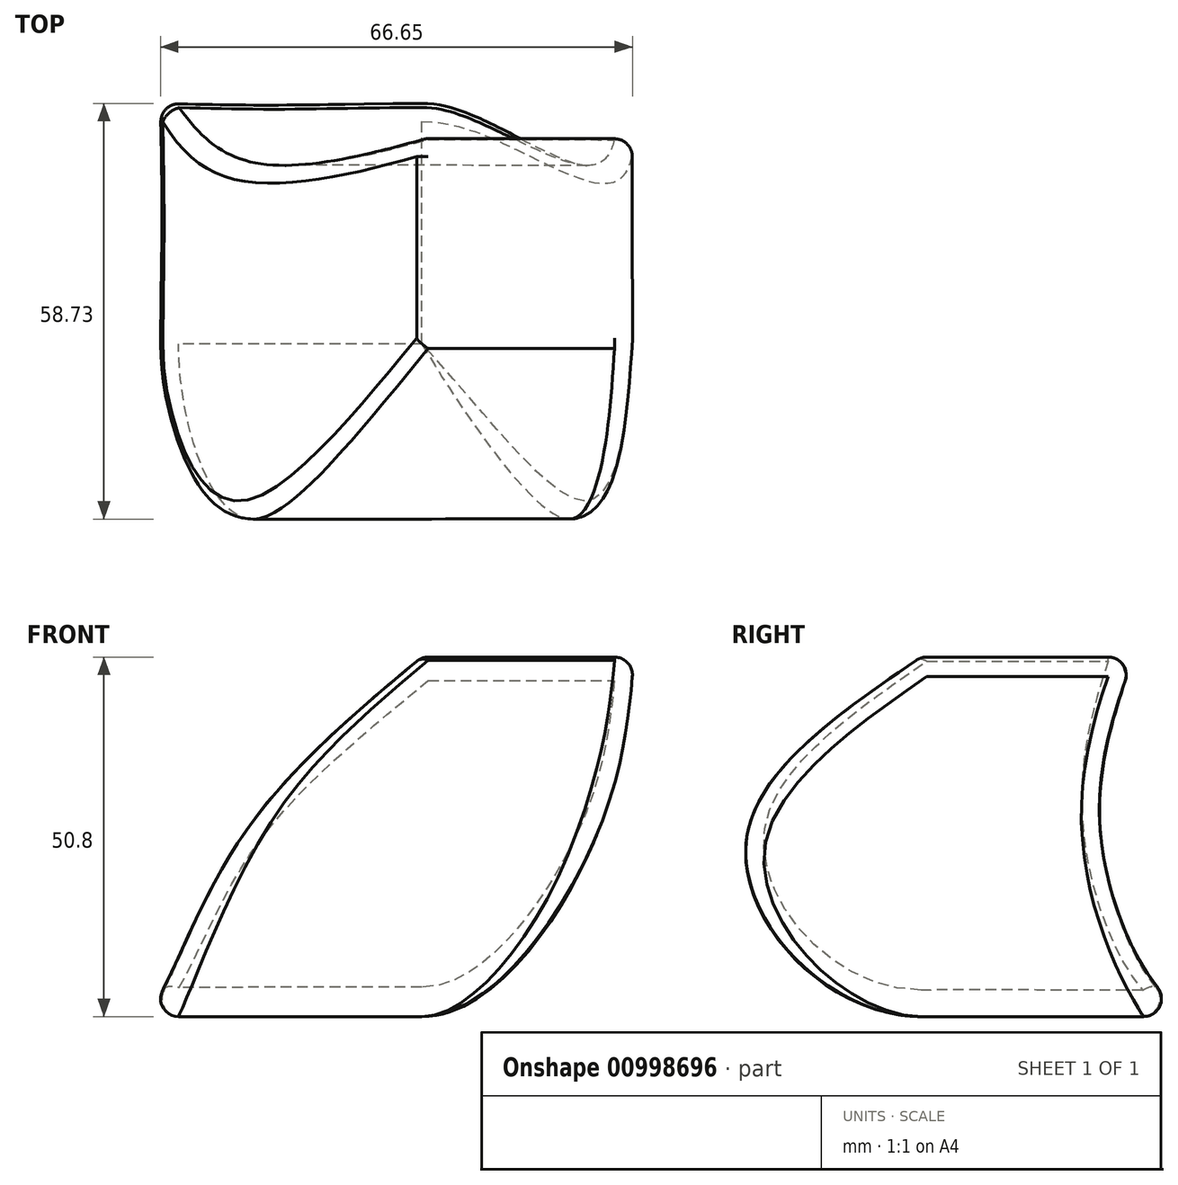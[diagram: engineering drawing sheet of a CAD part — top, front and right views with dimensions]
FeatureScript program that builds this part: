
annotation { "Feature Type Name" : "Feature", "Feature Type Description" : "" }
export const myFeature = defineFeature(function(context is Context, id is Id, definition is map)
    precondition{}
    {
        {
            var Q0;
            Q0=qCreatedBy(makeId("Top.planeOp"),FACE);
            var sketch = newSketch(context, id + "F0", { "sketchPlane" : qUnion([Q0])});
            skLineSegment(sketch, "E0.bottom", {"start": v(0, 0) * mm, "end": v(-40, 0) * mm});
            skLineSegment(sketch, "E0.top", {"start": v(0, 40) * mm, "end": v(-40, 40) * mm});
            skLineSegment(sketch, "E0.left", {"start": v(0, 0) * mm, "end": v(0, 40) * mm});
            skLineSegment(sketch, "E0.right", {"start": v(-40, 0) * mm, "end": v(-40, 40) * mm});
            skSolve(sketch);
        }
        {
            var Q0;
            Q0=qCreatedBy(makeId("Top.planeOp"),FACE);
            cPlane(context, id + "F1", {"entities" : qUnion([Q0]), "cplaneType" : CPlaneType.OFFSET, "offset" : 25.4 * mm, "width" : 152.4 * mm, "height" : 152.4 * mm});
        }
        {
            var Q0;
            Q0=qCreatedBy(id+"F1.planeOp",FACE);
            var sketch = newSketch(context, id + "F2", { "sketchPlane" : qUnion([Q0])});
            skLineSegment(sketch, "E1.bottom", {"start": v(-25.4, 25.4) * mm, "end": v(24.6, 25.4) * mm});
            skLineSegment(sketch, "E1.top", {"start": v(-25.4, -24.6) * mm, "end": v(24.6, -24.6) * mm});
            skLineSegment(sketch, "E1.left", {"start": v(-25.4, 25.4) * mm, "end": v(-25.4, -24.6) * mm});
            skLineSegment(sketch, "E1.right", {"start": v(24.6, 25.4) * mm, "end": v(24.6, -24.6) * mm});
            skSolve(sketch);
        }
        {
            var Q0;
            Q0=qCreatedBy(id+"F1.planeOp",FACE);
            cPlane(context, id + "F3", {"entities" : qUnion([Q0]), "cplaneType" : CPlaneType.OFFSET, "offset" : 25.4 * mm, "width" : 152.4 * mm, "height" : 152.4 * mm});
        }
        {
            var Q0;
            Q0=qCreatedBy(id+"F3.planeOp",FACE);
            var sketch = newSketch(context, id + "F4", { "sketchPlane" : qUnion([Q0])});
            skLineSegment(sketch, "E2.bottom", {"start": v(0, 0) * mm, "end": v(30, 0) * mm});
            skLineSegment(sketch, "E2.top", {"start": v(0, 30) * mm, "end": v(30, 30) * mm});
            skLineSegment(sketch, "E2.left", {"start": v(0, 0) * mm, "end": v(0, 30) * mm});
            skLineSegment(sketch, "E2.right", {"start": v(30, 0) * mm, "end": v(30, 30) * mm});
            skSolve(sketch);
        }
        {
            var Q0;
            Q0=makeQuery(id+"F0.imprint","IMPRINT",FACE,{"disambiguationData":[TD([[makeQuery(id+"F0.imprint","IMPRINT",EDGE,{"derivedFrom":sQuery(id+"F0.wireOp",EDGE,"E0.bottom")}),-1.0]])]});
            var Q1;
            Q1=makeQuery(id+"F2.imprint","IMPRINT",FACE,{"disambiguationData":[TD([[makeQuery(id+"F2.imprint","IMPRINT",EDGE,{"derivedFrom":sQuery(id+"F2.wireOp",EDGE,"E1.bottom")}),-1.0]])]});
            var Q2;
            Q2=makeQuery(id+"F4.imprint","IMPRINT",FACE,{"disambiguationData":[TD([[makeQuery(id+"F4.imprint","IMPRINT",EDGE,{"derivedFrom":sQuery(id+"F4.wireOp",EDGE,"E2.bottom")}),1.0]])]});
            loft(context, id + "F5", {"startCondition" : LoftEndDerivativeType.TANGENT_TO_PROFILE, "startMagnitude" : 1, "sheetProfilesArray" : [{ "sheetProfileEntities" : qUnion([Q0]) }, { "sheetProfileEntities" : qUnion([Q1]) }, { "sheetProfileEntities" : qUnion([Q2]) }]});
        }
        {
            var Q0;
            Q0=makeQuery(id+"F5.opLoft","SWEPT_EDGE",EDGE,{"disambiguationData":[OSD([sQuery(id+"F0.wireOp",EDGE,"E0.bottom"),sQuery(id+"F0.wireOp",EDGE,"E0.left"),sQuery(id+"F2.wireOp",EDGE,"E1.top"),sQuery(id+"F2.wireOp",EDGE,"E1.right"),sQuery(id+"F4.wireOp",EDGE,"E2.bottom"),sQuery(id+"F4.wireOp",EDGE,"E2.right")])]});
            var Q1;
            Q1=makeQuery(id+"F5.opLoft","SWEPT_EDGE",EDGE,{"disambiguationData":[OSD([sQuery(id+"F0.wireOp",EDGE,"E0.bottom"),sQuery(id+"F0.wireOp",EDGE,"E0.right"),sQuery(id+"F2.wireOp",EDGE,"E1.top"),sQuery(id+"F2.wireOp",EDGE,"E1.left"),sQuery(id+"F4.wireOp",EDGE,"E2.bottom"),sQuery(id+"F4.wireOp",EDGE,"E2.left")])]});
            var Q2;
            Q2=makeQuery(id+"F5.opLoft","SWEPT_EDGE",EDGE,{"disambiguationData":[OSD([sQuery(id+"F0.wireOp",EDGE,"E0.top"),sQuery(id+"F0.wireOp",EDGE,"E0.right"),sQuery(id+"F2.wireOp",EDGE,"E1.bottom"),sQuery(id+"F2.wireOp",EDGE,"E1.left"),sQuery(id+"F4.wireOp",EDGE,"E2.top"),sQuery(id+"F4.wireOp",EDGE,"E2.left")])]});
            var Q3;
            Q3=makeQuery(id+"F5.opLoft","SWEPT_EDGE",EDGE,{"disambiguationData":[OSD([sQuery(id+"F0.wireOp",EDGE,"E0.top"),sQuery(id+"F0.wireOp",EDGE,"E0.left"),sQuery(id+"F2.wireOp",EDGE,"E1.bottom"),sQuery(id+"F2.wireOp",EDGE,"E1.right"),sQuery(id+"F4.wireOp",EDGE,"E2.top"),sQuery(id+"F4.wireOp",EDGE,"E2.right")])]});
            var Q4;
            Q4=makeQuery(id+"F5.opLoft","MID_CAP_EDGE",EDGE,{"disambiguationData":[OSD([sQuery(id+"F4.wireOp",EDGE,"E2.bottom"),sQuery(id+"F4.wireOp",EDGE,"E2.top"),sQuery(id+"F4.wireOp",EDGE,"E2.right")])],"capPos":2.0});
            var Q5;
            Q5=makeQuery(id+"F5.opLoft","MID_CAP_EDGE",EDGE,{"disambiguationData":[OSD([sQuery(id+"F4.wireOp",EDGE,"E2.top"),sQuery(id+"F4.wireOp",EDGE,"E2.left"),sQuery(id+"F4.wireOp",EDGE,"E2.right")])],"capPos":2.0});
            var Q6;
            Q6=makeQuery(id+"F5.opLoft","MID_CAP_EDGE",EDGE,{"disambiguationData":[OSD([sQuery(id+"F4.wireOp",EDGE,"E2.bottom"),sQuery(id+"F4.wireOp",EDGE,"E2.top"),sQuery(id+"F4.wireOp",EDGE,"E2.left")])],"capPos":2.0});
            var Q7;
            Q7=makeQuery(id+"F5.opLoft","MID_CAP_EDGE",EDGE,{"disambiguationData":[OSD([sQuery(id+"F4.wireOp",EDGE,"E2.bottom"),sQuery(id+"F4.wireOp",EDGE,"E2.left"),sQuery(id+"F4.wireOp",EDGE,"E2.right")])],"capPos":2.0});
            var Q8;
            Q8=makeQuery(id+"F5.opLoft","CAP_FACE",FACE,{"disambiguationData":[OSD([makeQuery(id+"F0.imprint","IMPRINT",FACE,{"disambiguationData":[TD([[makeQuery(id+"F0.imprint","IMPRINT",EDGE,{"derivedFrom":sQuery(id+"F0.wireOp",EDGE,"E0.bottom")}),-1.0]])]})])],"isStart":true});
            fillet(context, id + "F6", {"entities" : qUnion([Q0, Q1, Q2, Q3, Q4, Q5, Q6, Q7, Q8]), "radius" : 2.54 * mm, "tangentPropagation" : true, "allowEdgeOverflow" : false});
        }
    });
